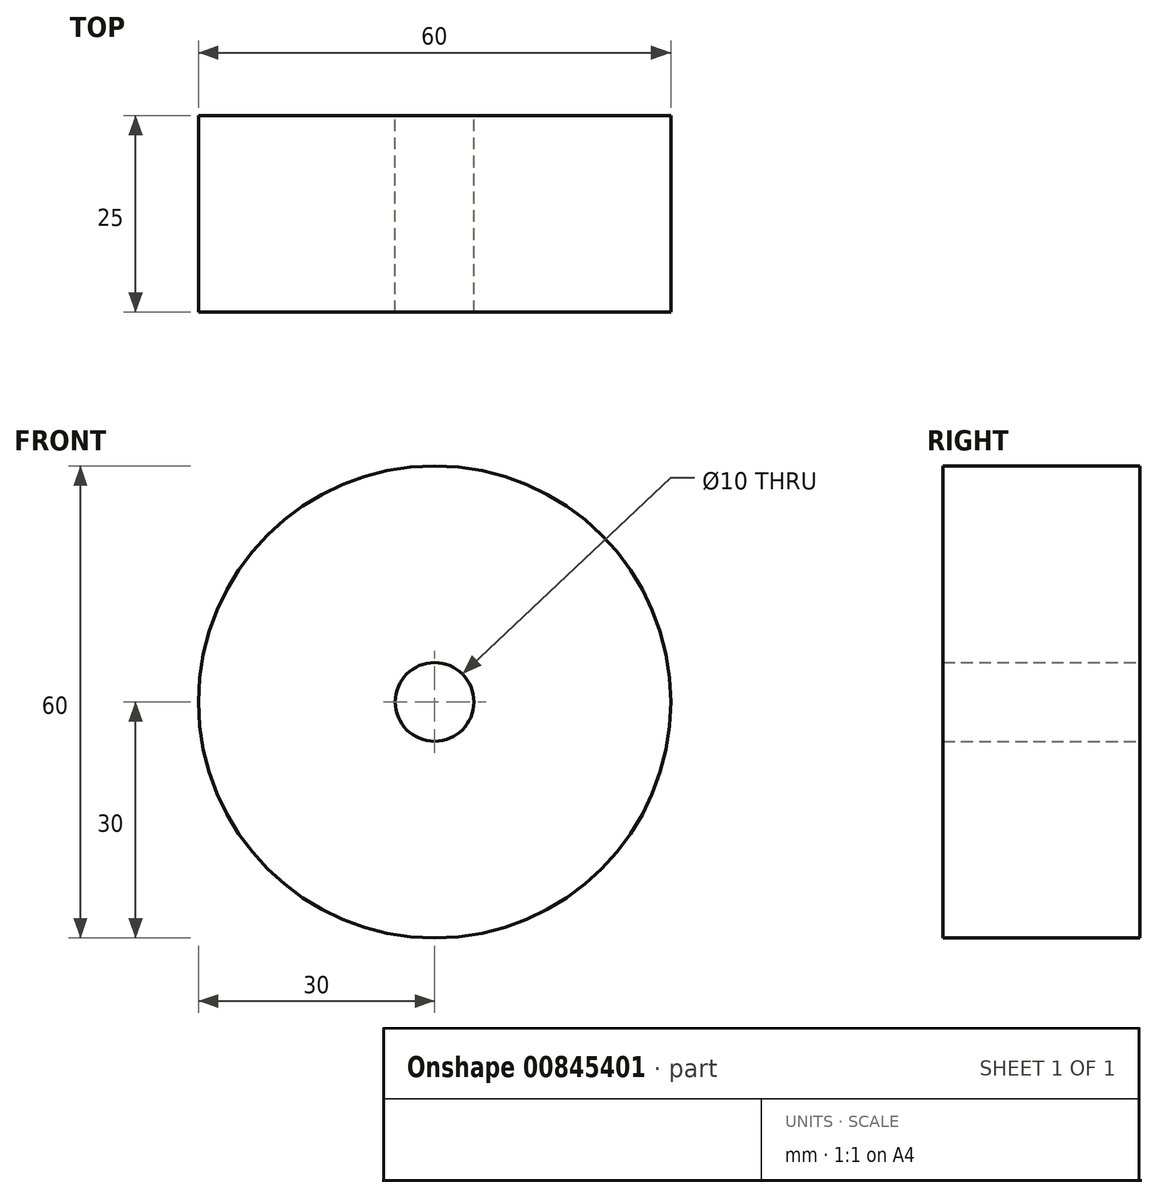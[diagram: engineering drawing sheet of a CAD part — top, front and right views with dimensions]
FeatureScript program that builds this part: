
annotation { "Feature Type Name" : "Feature", "Feature Type Description" : "" }
export const myFeature = defineFeature(function(context is Context, id is Id, definition is map)
    precondition{}
    {
        {
            var Q0;
            Q0=qCreatedBy(makeId("Front.planeOp"),FACE);
            var sketch = newSketch(context, id + "F0", { "sketchPlane" : qUnion([Q0])});
            skCircle(sketch, "E0", {"center": v(0, 0) * mm, "radius": 30 * mm});
            skCircle(sketch, "E1", {"center": v(0, 0) * mm, "radius": 5 * mm});
            skSolve(sketch);
        }
        {
            var Q0;
            Q0 = qSketchRegion(id + "F0", true);
            extrude(context, id + "F1", {"entities" : qUnion([Q0]), "depth" : 25 * mm, "offsetDistance" : 25 * mm});
        }
    });
